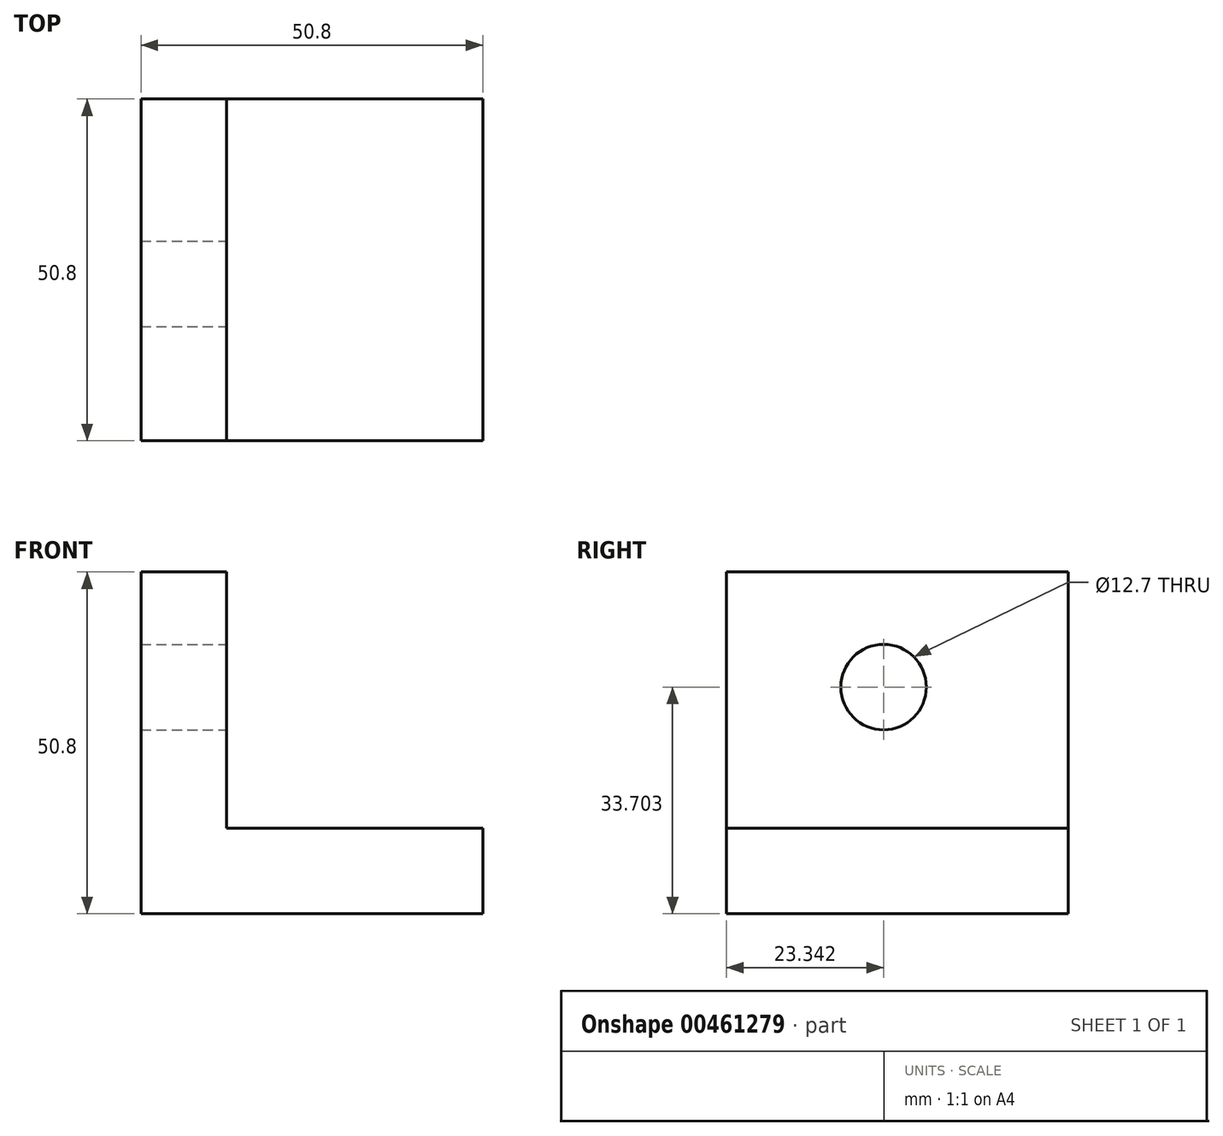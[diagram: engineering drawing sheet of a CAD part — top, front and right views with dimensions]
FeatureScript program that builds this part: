
annotation { "Feature Type Name" : "Feature", "Feature Type Description" : "" }
export const myFeature = defineFeature(function(context is Context, id is Id, definition is map)
    precondition{}
    {
        {
            var Q0;
            Q0=qCreatedBy(makeId("Top.planeOp"),FACE);
            var sketch = newSketch(context, id + "F0", { "sketchPlane" : qUnion([Q0])});
            skLineSegment(sketch, "E0.bottom", {"start": v(-18.28, 32.39) * mm, "end": v(32.52, 32.39) * mm});
            skLineSegment(sketch, "E0.top", {"start": v(-18.28, -18.41) * mm, "end": v(32.52, -18.41) * mm});
            skLineSegment(sketch, "E0.left", {"start": v(-18.28, 32.39) * mm, "end": v(-18.28, -18.41) * mm});
            skLineSegment(sketch, "E0.right", {"start": v(32.52, 32.39) * mm, "end": v(32.52, -18.41) * mm});
            skLineSegment(sketch, "E1.0", {"start": v(-5.58, 32.39) * mm, "end": v(-5.58, -18.41) * mm});
            skSolve(sketch);
        }
        {
            var Q0;
            Q0=makeQuery(id+"F0.imprint","IMPRINT",FACE,{"disambiguationData":[TD([[makeQuery(id+"F0.imprint","IMPRINT",EDGE,{"derivedFrom":sQuery(id+"F0.wireOp",EDGE,"E0.bottom")}),-1.0]])]});
            extrude(context, id + "F1", {"entities" : qUnion([Q0]), "depth" : 12.7 * mm});
        }
        {
            var Q0;
            {var subQ0=sQuery(id+"F0.wireOp",EDGE,"E0.left");Q0=makeQuery(id+"F0.imprint","IMPRINT",FACE,{"disambiguationData":[TD([[makeQuery(id+"F0.imprint","IMPRINT",EDGE,{"derivedFrom":subQ0}),1.0]])]});}
            extrude(context, id + "F2", {"entities" : qUnion([Q0]), "operationType" : NewBodyOperationType.ADD, "depth" : 50.8 * mm});
        }
        {
            var Q0;
            Q0=makeQuery(id+"F2.opExtrude","SWEPT_FACE",FACE,{"disambiguationData":[OSD([sQuery(id+"F0.wireOp",EDGE,"E1.0")])]});
            var sketch = newSketch(context, id + "F3", { "sketchPlane" : qUnion([Q0])});
            skCircle(sketch, "E2", {"center": v(4.93, 33.7) * mm, "radius": 6.35 * mm});
            skSolve(sketch);
        }
        {
            var Q0;
            Q0=makeQuery(id+"F3.imprint","IMPRINT",FACE,{"disambiguationData":[TD([[makeQuery(id+"F3.imprint","IMPRINT",EDGE,{"derivedFrom":sQuery(id+"F3.wireOp",EDGE,"E2")}),1.0]])]});
            extrude(context, id + "F4", {"entities" : qUnion([Q0]), "operationType" : NewBodyOperationType.REMOVE, "endBound" : BoundingType.THROUGH_ALL, "oppositeDirection" : true, "depth" : 25.4 * mm});
        }
    });
